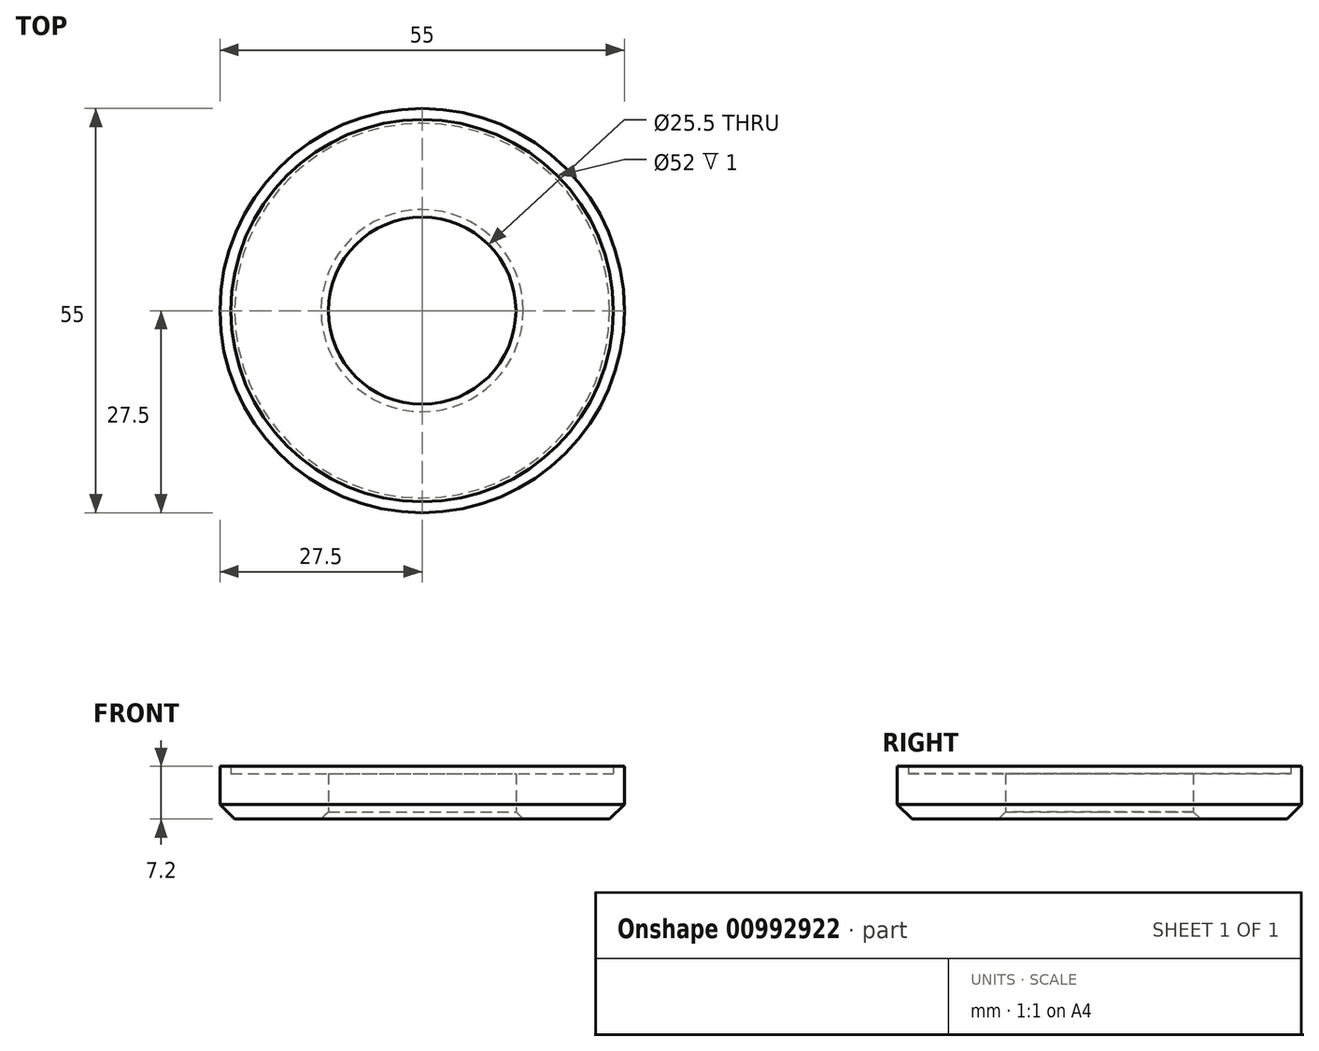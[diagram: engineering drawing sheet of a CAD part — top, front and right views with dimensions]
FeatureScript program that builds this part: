
annotation { "Feature Type Name" : "Feature", "Feature Type Description" : "" }
export const myFeature = defineFeature(function(context is Context, id is Id, definition is map)
    precondition{}
    {
        {
            var Q0;
            Q0=qCreatedBy(makeId("Front.planeOp"),FACE);
            var sketch = newSketch(context, id + "F0", { "sketchPlane" : qUnion([Q0])});
            skLineSegment(sketch, "E0", {"start": v(0, 0) * mm, "end": v(0, 30.78) * mm, "construction": true});
            skLineSegment(sketch, "E1", {"start": v(12.75, 0) * mm, "end": v(27.5, 0) * mm});
            skLineSegment(sketch, "E2", {"start": v(27.5, 0) * mm, "end": v(27.5, 7.2) * mm});
            skLineSegment(sketch, "E3", {"start": v(27.5, 7.2) * mm, "end": v(26, 7.2) * mm});
            skLineSegment(sketch, "E4", {"start": v(26, 7.2) * mm, "end": v(26, 6.2) * mm});
            skLineSegment(sketch, "E5", {"start": v(26, 6.2) * mm, "end": v(12.75, 6.2) * mm});
            skLineSegment(sketch, "E6", {"start": v(12.75, 6.2) * mm, "end": v(12.75, 0) * mm});
            skSolve(sketch);
        }
        {
            var Q0;
            Q0=makeQuery(id+"F0.imprint","IMPRINT",FACE,{"disambiguationData":[TD([[makeQuery(id+"F0.imprint","IMPRINT",EDGE,{"derivedFrom":sQuery(id+"F0.wireOp",EDGE,"E1")}),1.0]])]});
            var Q1;
            Q1=sQuery(id+"F0.wireOp",EDGE,"E0");
            revolve(context, id + "F1", {"surfaceOperationType" : NewSurfaceOperationType.NEW, "entities" : qUnion([Q0]), "axis" : qUnion([Q1]), "revolveType" : RevolveType.FULL});
        }
        {
            var Q0;
            Q0=makeQuery(id+"F1.opRevolve","SWEPT_EDGE",EDGE,{"disambiguationData":[OSD([sQuery(id+"F0.wireOp",EDGE,"E1"),sQuery(id+"F0.wireOp",EDGE,"E2")])]});
            chamfer(context, id + "F2", {"entities" : qUnion([Q0]), "width" : 2 * mm, "tangentPropagation" : true});
        }
        {
            var Q0;
            Q0=makeQuery(id+"F1.opRevolve","SWEPT_EDGE",EDGE,{"disambiguationData":[OSD([sQuery(id+"F0.wireOp",EDGE,"E1"),sQuery(id+"F0.wireOp",EDGE,"E6")])]});
            chamfer(context, id + "F3", {"entities" : qUnion([Q0]), "width" : 1 * mm, "tangentPropagation" : true});
        }
    });
